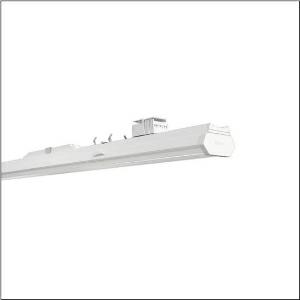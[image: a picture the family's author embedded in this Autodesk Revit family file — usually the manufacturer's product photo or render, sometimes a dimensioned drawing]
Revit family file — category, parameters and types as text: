
# Revit family: licross_r__11_protected_mo_51td12dn495g_4259
name_source: partatom
category: Lighting Fixtures
units: mm (PartAtom-declared; Revit-internal decimal feet)

## family parameters
Cut with Voids When Loaded = No
Host = Face
Light Source = No
Part Type = Normal
Room Calculation Point = No
Round Connector Dimension = Use Diameter
Shared = No

## types (1)
- --- (1 x LED, 9980 lm, 57.1 W, 4000K)
    Apparent Load = 57 VA
    CIE Flux Codes = 73 92 98 99 100
    Color Rendering = 80
    Color Temperature = 4000K
    Default Elevation = 1800 mm
    Description = Licross® 11 Protected MO, luminaire insert, of sheet steel, galvanised, coil coated, white, length: 1.500mm, width: 90mm, height: 101mm, LED rated luminous flux: 9.980lm, light colour: 840, control gear: DALI 2, with plug, 5-pole, with phase selection, mains connection: 220..240V, AC, 50/60Hz, rated input power: 57W, halogen-free wiring, primary optical cover: cover, of PMMA, light emission: direct distribution, primary light characteristic: symmetric, protection rating (complete): IP54, insulation class (complete): insulation class I (protective earthing), certification: CE, ENEC, VDE, UKCA, protection symbol: D if used in an environment with non-conductive dust loads with corresponding accessories, impact resistance: IK06, permissible ambient temperature for indoor applications: -25..+35°C, corresponds to IFS (International Featured Standards) requirements for safety and quality in the food industry, reducing of maximum allowable ambient temperature of 5°C with ceiling mounting, LABS conformity tested according to VDMA 24364:2018-05, packaging unit: 1 piece
    Height = 92 mm
    Lamp = 1 x LED
    Lamp Light Flux = 9980 lm
    Lamp Power = 57.1 W
    Lamp count = 1
    Length = 1500 mm
    Luminous efficacy = 175 lm/W
    Manufacturer = Siteco
    ModVariant = No
    Model = 51TD12DN495G
    Mounting Place = Ceiling
    Mounting Type = Pendant
    Number of Poles = 1
    OnlyDefault = Yes
    Power Factor = 1
    Product Name = Licross® 11 Protected MO
    Product group = luminaire insert
    ProductGroupID = 901
    Protection Class = Protection class I
    Protection Degree = IP 54
    RLX_Detail_Level = 1
    RLX_Emergency_Light_Flux = 0 lm
    RLX_Emergency_Type = 0
    RLX_Emergency_Type_DB = No
    RlxData = <blob elided: 24429 chars, md5=e5eee745>
    Socket = socket
    Standby Power = 0 W
    System Light Flux = 9980 lm
    System Power = 57 W
    Type Comments = factory setting: luminous flux: 100 % | dim-lin: 254 | 378 mA
    Type Image = l_1256145.jpg
    URL = http://relux.com
    VarID = @adj_098578
    Voltage = 0 V
    Weight = 0.00 kg
    Width = 88 mm

## geometry (parser evidence)
native form markers: Blend x4, Sweep x10
no freeform markers — native parametric forms only
